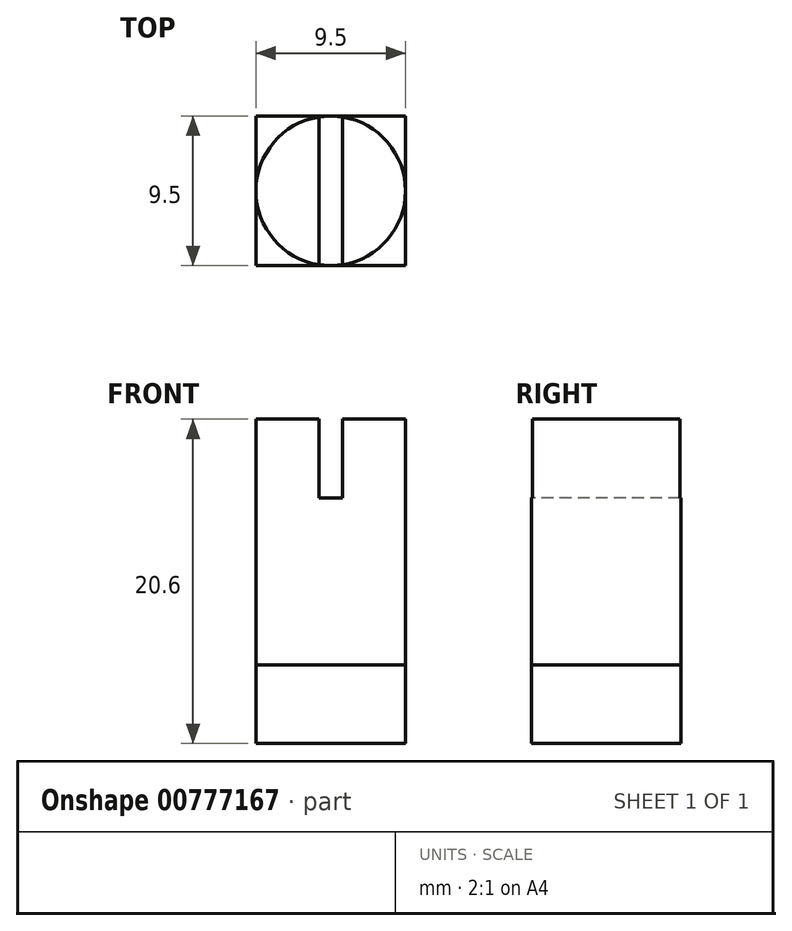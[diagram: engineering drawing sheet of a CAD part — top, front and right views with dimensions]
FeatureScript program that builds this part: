
annotation { "Feature Type Name" : "Feature", "Feature Type Description" : "" }
export const myFeature = defineFeature(function(context is Context, id is Id, definition is map)
    precondition{}
    {
        {
            var Q0;
            Q0=qCreatedBy(makeId("Top.planeOp"),FACE);
            var sketch = newSketch(context, id + "F0", { "sketchPlane" : qUnion([Q0])});
            skCircle(sketch, "E0", {"center": v(0, 0) * mm, "radius": 4.75 * mm});
            skSolve(sketch);
        }
        {
            var Q0;
            Q0=qSketchRegion(id+"F0",true);
            extrude(context, id + "F1", {"entities" : qUnion([Q0]), "depth" : 20.6 * mm, "offsetDistance" : 25.4 * mm});
        }
        {
            var Q0;
            Q0=qCreatedBy(makeId("Top.planeOp"),FACE);
            cPlane(context, id + "F2", {"entities" : qUnion([Q0]), "cplaneType" : CPlaneType.OFFSET, "offset" : 20.6 * mm, "width" : 152.4 * mm, "height" : 152.4 * mm});
        }
        {
            var Q0;
            Q0=qCreatedBy(id+"F2.planeOp",FACE);
            var sketch = newSketch(context, id + "F3", { "sketchPlane" : qUnion([Q0])});
            skLineSegment(sketch, "E1.bottom", {"start": v(0.75, 5.36) * mm, "end": v(-0.75, 5.36) * mm});
            skLineSegment(sketch, "E1.top", {"start": v(0.75, -5.36) * mm, "end": v(-0.75, -5.36) * mm});
            skLineSegment(sketch, "E1.left", {"start": v(0.75, 5.36) * mm, "end": v(0.75, -5.36) * mm});
            skLineSegment(sketch, "E1.right", {"start": v(-0.75, 5.36) * mm, "end": v(-0.75, -5.36) * mm});
            skPoint(sketch, "E1.middle", {"position": v(0, 0) * mm});
            skSolve(sketch);
        }
        {
            var Q0;
            Q0=qSketchRegion(id+"F3",true);
            extrude(context, id + "F4", {"entities" : qUnion([Q0]), "operationType" : NewBodyOperationType.REMOVE, "oppositeDirection" : true, "depth" : 5 * mm, "offsetDistance" : 25.4 * mm});
        }
        {
            var Q0;
            Q0=qCreatedBy(makeId("Top.planeOp"),FACE);
            var sketch = newSketch(context, id + "F5", { "sketchPlane" : qUnion([Q0])});
            skLineSegment(sketch, "E2.bottom", {"start": v(4.75, 4.75) * mm, "end": v(-4.75, 4.75) * mm});
            skLineSegment(sketch, "E2.top", {"start": v(4.75, -4.75) * mm, "end": v(-4.75, -4.75) * mm});
            skLineSegment(sketch, "E2.left", {"start": v(4.75, 4.75) * mm, "end": v(4.75, -4.75) * mm});
            skLineSegment(sketch, "E2.right", {"start": v(-4.75, 4.75) * mm, "end": v(-4.75, -4.75) * mm});
            skPoint(sketch, "E2.middle", {"position": v(0, 0) * mm});
            skSolve(sketch);
        }
        {
            var Q0;
            Q0=qSketchRegion(id+"F5",true);
            extrude(context, id + "F6", {"entities" : qUnion([Q0]), "operationType" : NewBodyOperationType.ADD, "depth" : 5 * mm, "offsetDistance" : 25.4 * mm});
        }
    });
